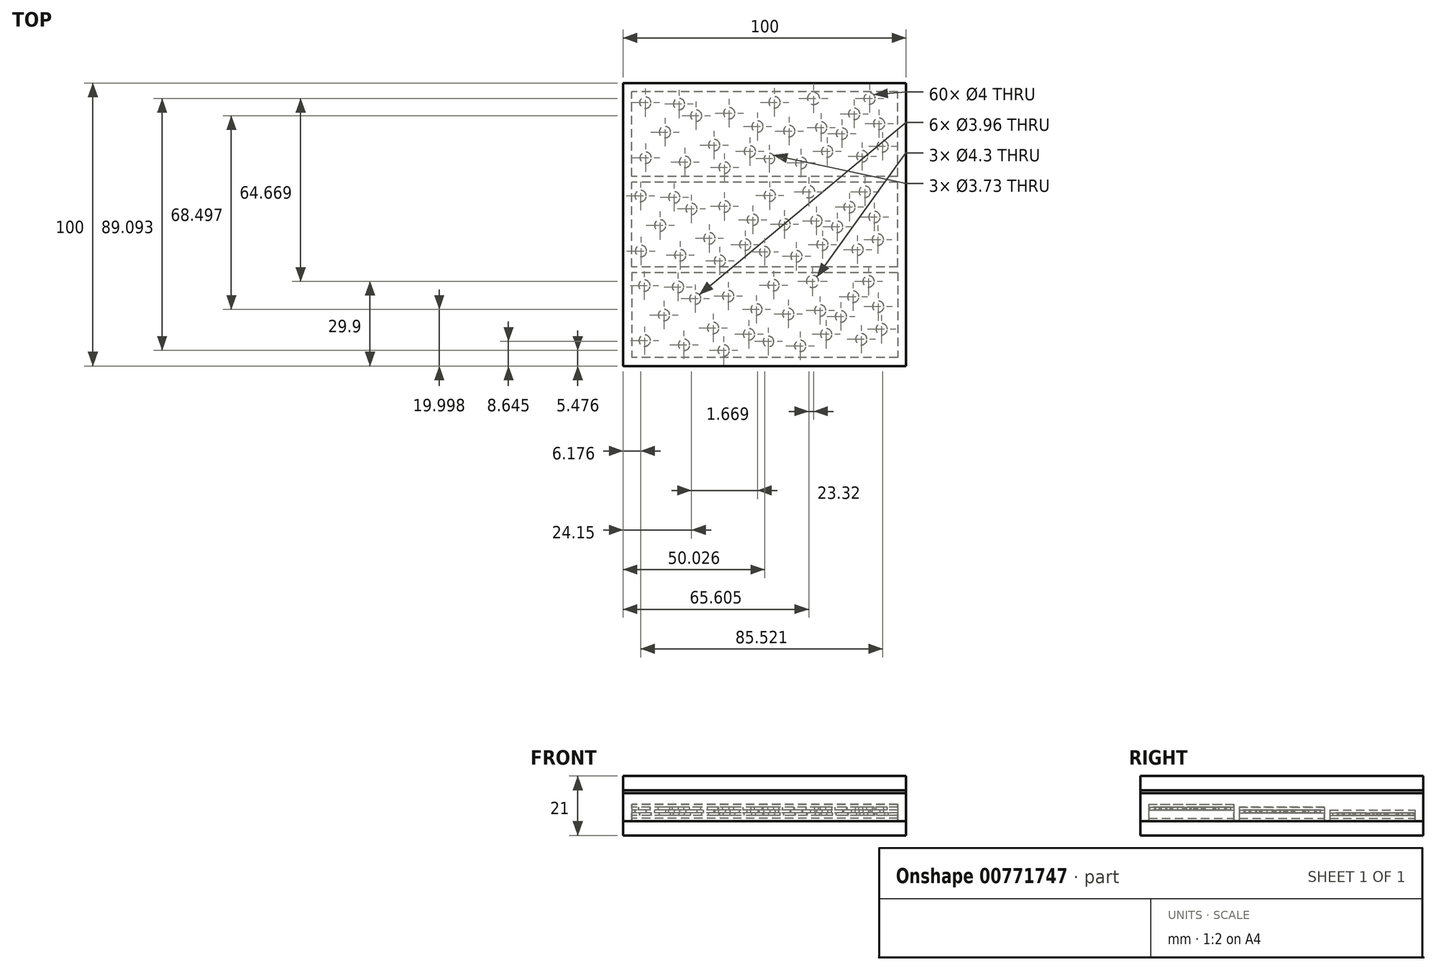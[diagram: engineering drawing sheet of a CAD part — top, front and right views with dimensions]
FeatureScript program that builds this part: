
annotation { "Feature Type Name" : "Feature", "Feature Type Description" : "" }
export const myFeature = defineFeature(function(context is Context, id is Id, definition is map)
    precondition{}
    {
        {
            var Q0;
            Q0=qCreatedBy(makeId("Top.planeOp"),FACE);
            var sketch = newSketch(context, id + "F0", { "sketchPlane" : qUnion([Q0])});
            skLineSegment(sketch, "E0.bottom", {"start": v(50, -50) * mm, "end": v(-50, -50) * mm});
            skLineSegment(sketch, "E0.top", {"start": v(50, 50) * mm, "end": v(-50, 50) * mm});
            skLineSegment(sketch, "E0.left", {"start": v(50, -50) * mm, "end": v(50, 50) * mm});
            skLineSegment(sketch, "E0.right", {"start": v(-50, -50) * mm, "end": v(-50, 50) * mm});
            skPoint(sketch, "E0.middle", {"position": v(0, 0) * mm});
            skSolve(sketch);
        }
        {
            var Q0;
            Q0=makeQuery(id+"F0.imprint","IMPRINT",FACE,{"disambiguationData":[TD([[makeQuery(id+"F0.imprint","IMPRINT",EDGE,{"derivedFrom":sQuery(id+"F0.wireOp",EDGE,"E0.bottom")}),-1.0]])]});
            extrude(context, id + "F1", {"entities" : qUnion([Q0]), "depth" : 5 * mm, "offsetDistance" : 25 * mm});
        }
        {
            var Q0;
            Q0=makeQuery(id+"F1.opExtrude","CAP_FACE",FACE,{"disambiguationData":[OSD([sQuery(id+"F0.wireOp",EDGE,"E0.bottom"),sQuery(id+"F0.wireOp",EDGE,"E0.top"),sQuery(id+"F0.wireOp",EDGE,"E0.left"),sQuery(id+"F0.wireOp",EDGE,"E0.right")])],"isStart":false});
            var sketch = newSketch(context, id + "F2", { "sketchPlane" : qUnion([Q0])});
            skLineSegment(sketch, "E1.bottom", {"start": v(47, -15) * mm, "end": v(-47, -15) * mm});
            skLineSegment(sketch, "E1.top", {"start": v(47, 15) * mm, "end": v(-47, 15) * mm});
            skLineSegment(sketch, "E1.left", {"start": v(47, -15) * mm, "end": v(47, 15) * mm});
            skLineSegment(sketch, "E1.right", {"start": v(-47, -15) * mm, "end": v(-47, 15) * mm});
            skPoint(sketch, "E1.middle", {"position": v(0, 0) * mm});
            skLineSegment(sketch, "E2.bottom", {"start": v(47, 17) * mm, "end": v(-47, 17) * mm});
            skLineSegment(sketch, "E2.top", {"start": v(47, 47) * mm, "end": v(-47, 47) * mm});
            skLineSegment(sketch, "E2.left", {"start": v(47, 17) * mm, "end": v(47, 47) * mm});
            skLineSegment(sketch, "E2.right", {"start": v(-47, 17) * mm, "end": v(-47, 47) * mm});
            skPoint(sketch, "E2.middle", {"position": v(0, 32) * mm});
            skLineSegment(sketch, "E3.bottom", {"start": v(47, -47) * mm, "end": v(-47, -47) * mm});
            skLineSegment(sketch, "E3.top", {"start": v(47, -17) * mm, "end": v(-47, -17) * mm});
            skLineSegment(sketch, "E3.left", {"start": v(47, -47) * mm, "end": v(47, -17) * mm});
            skLineSegment(sketch, "E3.right", {"start": v(-47, -47) * mm, "end": v(-47, -17) * mm});
            skPoint(sketch, "E3.middle", {"position": v(0, -32) * mm});
            skSolve(sketch);
        }
        {
            var Q0;
            Q0=makeQuery(id+"F2.imprint","IMPRINT",FACE,{"disambiguationData":[TD([[makeQuery(id+"F2.imprint","IMPRINT",EDGE,{"derivedFrom":sQuery(id+"F2.wireOp",EDGE,"E2.bottom")}),-1.0]])]});
            var Q1;
            Q1=makeQuery(id+"F2.imprint","IMPRINT",FACE,{"disambiguationData":[TD([[makeQuery(id+"F2.imprint","IMPRINT",EDGE,{"derivedFrom":sQuery(id+"F2.wireOp",EDGE,"E1.bottom")}),-1.0]])]});
            var Q2;
            Q2=makeQuery(id+"F2.imprint","IMPRINT",FACE,{"disambiguationData":[TD([[makeQuery(id+"F2.imprint","IMPRINT",EDGE,{"derivedFrom":sQuery(id+"F2.wireOp",EDGE,"E3.bottom")}),-1.0]])]});
            extrude(context, id + "F3", {"entities" : qUnion([Q0, Q1, Q2]), "depth" : 1 * mm, "offsetDistance" : 25 * mm});
        }
        {
            var Q0;
            Q0=makeQuery(id+"F3.opExtrude","CAP_FACE",FACE,{"disambiguationData":[OSD([sQuery(id+"F2.wireOp",EDGE,"E2.bottom"),sQuery(id+"F2.wireOp",EDGE,"E2.top"),sQuery(id+"F2.wireOp",EDGE,"E2.left"),sQuery(id+"F2.wireOp",EDGE,"E2.right")])],"isStart":false});
            extrude(context, id + "F4", {"entities" : qUnion([Q0]), "depth" : 1 * mm, "offsetDistance" : 25 * mm});
        }
        {
            var Q0;
            Q0=makeQuery(id+"F3.opExtrude","CAP_FACE",FACE,{"disambiguationData":[OSD([sQuery(id+"F2.wireOp",EDGE,"E1.bottom"),sQuery(id+"F2.wireOp",EDGE,"E1.top"),sQuery(id+"F2.wireOp",EDGE,"E1.left"),sQuery(id+"F2.wireOp",EDGE,"E1.right")])],"isStart":false});
            extrude(context, id + "F5", {"entities" : qUnion([Q0]), "depth" : 2 * mm, "offsetDistance" : 25 * mm});
        }
        {
            var Q0;
            Q0=makeQuery(id+"F3.opExtrude","CAP_FACE",FACE,{"disambiguationData":[OSD([sQuery(id+"F2.wireOp",EDGE,"E3.bottom"),sQuery(id+"F2.wireOp",EDGE,"E3.top"),sQuery(id+"F2.wireOp",EDGE,"E3.left"),sQuery(id+"F2.wireOp",EDGE,"E3.right")])],"isStart":false});
            extrude(context, id + "F6", {"entities" : qUnion([Q0]), "depth" : 3 * mm, "offsetDistance" : 25 * mm});
        }
        {
            var Q0;
            Q0=makeQuery(id+"F6.opExtrude","CAP_FACE",FACE,{"disambiguationData":[OSD([sQuery(id+"F2.wireOp",EDGE,"E3.bottom"),sQuery(id+"F2.wireOp",EDGE,"E3.top"),sQuery(id+"F2.wireOp",EDGE,"E3.left"),sQuery(id+"F2.wireOp",EDGE,"E3.right")])],"isStart":false});
            var Q1;
            Q1=makeQuery(id+"F5.opExtrude","CAP_FACE",FACE,{"disambiguationData":[OSD([sQuery(id+"F2.wireOp",EDGE,"E1.bottom"),sQuery(id+"F2.wireOp",EDGE,"E1.top"),sQuery(id+"F2.wireOp",EDGE,"E1.left"),sQuery(id+"F2.wireOp",EDGE,"E1.right")])],"isStart":false});
            var Q2;
            Q2=makeQuery(id+"F4.opExtrude","CAP_FACE",FACE,{"disambiguationData":[OSD([sQuery(id+"F2.wireOp",EDGE,"E2.bottom"),sQuery(id+"F2.wireOp",EDGE,"E2.top"),sQuery(id+"F2.wireOp",EDGE,"E2.left"),sQuery(id+"F2.wireOp",EDGE,"E2.right")])],"isStart":false});
            extrude(context, id + "F7", {"entities" : qUnion([Q0, Q1, Q2]), "depth" : 1 * mm, "offsetDistance" : 25 * mm});
        }
        {
            var Q0;
            Q0=makeQuery(id+"F7.opExtrude","CAP_FACE",FACE,{"disambiguationData":[OSD([sQuery(id+"F2.wireOp",EDGE,"E3.bottom"),sQuery(id+"F2.wireOp",EDGE,"E3.top"),sQuery(id+"F2.wireOp",EDGE,"E3.left"),sQuery(id+"F2.wireOp",EDGE,"E3.right")])],"isStart":false});
            var sketch = newSketch(context, id + "F8", { "sketchPlane" : qUnion([Q0])});
            skCircle(sketch, "E4", {"center": v(-35.55, -32) * mm, "radius": 2 * mm});
            skCircle(sketch, "E5", {"center": v(-18.19, -36.58) * mm, "radius": 2 * mm});
            skCircle(sketch, "E6", {"center": v(-12.85, -25.3) * mm, "radius": 2 * mm});
            skCircle(sketch, "E7", {"center": v(8.36, -31.62) * mm, "radius": 2 * mm});
            skCircle(sketch, "E8", {"center": v(19.64, -30.38) * mm, "radius": 2 * mm});
            skCircle(sketch, "E9", {"center": v(31.3, -25.54) * mm, "radius": 2 * mm});
            skCircle(sketch, "E10", {"center": v(34.16, -40.55) * mm, "radius": 2 * mm});
            skCircle(sketch, "E11", {"center": v(12.57, -42.9) * mm, "radius": 2 * mm});
            skCircle(sketch, "E12", {"center": v(3.15, -21.45) * mm, "radius": 2 * mm});
            skCircle(sketch, "E13", {"center": v(-5.53, -38.81) * mm, "radius": 2 * mm});
            skCircle(sketch, "E14", {"center": v(-30.59, -22.07) * mm, "radius": 2 * mm});
            skCircle(sketch, "E15", {"center": v(-42.37, -41.05) * mm, "radius": 2 * mm});
            skCircle(sketch, "E16", {"center": v(40.11, -29.01) * mm, "radius": 2 * mm});
            skCircle(sketch, "E17", {"center": v(-28.48, -42.53) * mm, "radius": 2 * mm});
            skCircle(sketch, "E18", {"center": v(21.75, -38.81) * mm, "radius": 2 * mm});
            skCircle(sketch, "E19", {"center": v(-42.5, -21.57) * mm, "radius": 2 * mm});
            skCircle(sketch, "E20", {"center": v(-2.87, -30) * mm, "radius": 1.98 * mm});
            skCircle(sketch, "E21", {"center": v(16.93, -20.1) * mm, "radius": 2.15 * mm});
            skCircle(sketch, "E22", {"center": v(-24.52, -26.17) * mm, "radius": 1.98 * mm});
            skCircle(sketch, "E23", {"center": v(36.73, -20.1) * mm, "radius": 2 * mm});
            skCircle(sketch, "E24", {"center": v(41.36, -37) * mm, "radius": 2 * mm});
            skCircle(sketch, "E25", {"center": v(26.97, -32.5) * mm, "radius": 2 * mm});
            skCircle(sketch, "E26", {"center": v(1.35, -41.36) * mm, "radius": 1.87 * mm});
            skCircle(sketch, "E27", {"center": v(-14.49, -44.52) * mm, "radius": 2 * mm});
            skSolve(sketch);
        }
        {
            var Q0;
            Q0=qSketchRegion(id+"F8",true);
            extrude(context, id + "F9", {"entities" : qUnion([Q0]), "operationType" : NewBodyOperationType.REMOVE, "oppositeDirection" : true, "depth" : 1 * mm, "offsetDistance" : 25 * mm});
        }
        {
            var Q0;
            Q0=makeQuery(id+"F7.opExtrude","CAP_FACE",FACE,{"disambiguationData":[OSD([sQuery(id+"F2.wireOp",EDGE,"E1.bottom"),sQuery(id+"F2.wireOp",EDGE,"E1.top"),sQuery(id+"F2.wireOp",EDGE,"E1.left"),sQuery(id+"F2.wireOp",EDGE,"E1.right")])],"isStart":false});
            var sketch = newSketch(context, id + "F10", { "sketchPlane" : qUnion([Q0])});
            skCircle(sketch, "E28", {"center": v(-36.88, -0.3) * mm, "radius": 2 * mm});
            skCircle(sketch, "E29", {"center": v(-19.51, -4.9) * mm, "radius": 2 * mm});
            skCircle(sketch, "E30", {"center": v(-14.18, 6.4) * mm, "radius": 2 * mm});
            skCircle(sketch, "E31", {"center": v(7.03, 0.07) * mm, "radius": 2 * mm});
            skCircle(sketch, "E32", {"center": v(18.32, 1.3) * mm, "radius": 2 * mm});
            skCircle(sketch, "E33", {"center": v(29.98, 6.15) * mm, "radius": 2 * mm});
            skCircle(sketch, "E34", {"center": v(32.83, -8.86) * mm, "radius": 2 * mm});
            skCircle(sketch, "E35", {"center": v(11.25, -11.22) * mm, "radius": 2 * mm});
            skCircle(sketch, "E36", {"center": v(1.82, 10.24) * mm, "radius": 2 * mm});
            skCircle(sketch, "E37", {"center": v(-6.86, -7.13) * mm, "radius": 2 * mm});
            skCircle(sketch, "E38", {"center": v(-31.92, 9.62) * mm, "radius": 2 * mm});
            skCircle(sketch, "E39", {"center": v(-43.7, -9.36) * mm, "radius": 2 * mm});
            skCircle(sketch, "E40", {"center": v(38.78, 2.67) * mm, "radius": 2 * mm});
            skCircle(sketch, "E41", {"center": v(-29.8, -10.85) * mm, "radius": 2 * mm});
            skCircle(sketch, "E42", {"center": v(20.43, -7.13) * mm, "radius": 2 * mm});
            skCircle(sketch, "E43", {"center": v(-43.82, 10.12) * mm, "radius": 2 * mm});
            skCircle(sketch, "E44", {"center": v(-4.2, 1.69) * mm, "radius": 1.98 * mm});
            skCircle(sketch, "E45", {"center": v(15.6, 11.59) * mm, "radius": 2.15 * mm});
            skCircle(sketch, "E46", {"center": v(-25.85, 5.52) * mm, "radius": 1.98 * mm});
            skCircle(sketch, "E47", {"center": v(35.4, 11.59) * mm, "radius": 2 * mm});
            skCircle(sketch, "E48", {"center": v(40.03, -5.31) * mm, "radius": 2 * mm});
            skCircle(sketch, "E49", {"center": v(25.64, -0.82) * mm, "radius": 2 * mm});
            skCircle(sketch, "E50", {"center": v(0.03, -9.67) * mm, "radius": 1.87 * mm});
            skCircle(sketch, "E51", {"center": v(-15.82, -12.84) * mm, "radius": 2 * mm});
            skSolve(sketch);
        }
        {
            var Q0;
            Q0=qSketchRegion(id+"F10",true);
            extrude(context, id + "F11", {"entities" : qUnion([Q0]), "operationType" : NewBodyOperationType.REMOVE, "oppositeDirection" : true, "depth" : 1 * mm, "offsetDistance" : 25 * mm});
        }
        {
            var Q0;
            Q0=makeQuery(id+"F7.opExtrude","CAP_FACE",FACE,{"disambiguationData":[OSD([sQuery(id+"F2.wireOp",EDGE,"E2.bottom"),sQuery(id+"F2.wireOp",EDGE,"E2.top"),sQuery(id+"F2.wireOp",EDGE,"E2.left"),sQuery(id+"F2.wireOp",EDGE,"E2.right")])],"isStart":false});
            var sketch = newSketch(context, id + "F12", { "sketchPlane" : qUnion([Q0])});
            skCircle(sketch, "E52", {"center": v(-35.2, 32.68) * mm, "radius": 2 * mm});
            skCircle(sketch, "E53", {"center": v(-17.84, 28.09) * mm, "radius": 2 * mm});
            skCircle(sketch, "E54", {"center": v(-12.51, 39.38) * mm, "radius": 2 * mm});
            skCircle(sketch, "E55", {"center": v(8.7, 33.05) * mm, "radius": 2 * mm});
            skCircle(sketch, "E56", {"center": v(19.99, 34.29) * mm, "radius": 2 * mm});
            skCircle(sketch, "E57", {"center": v(31.65, 39.13) * mm, "radius": 2 * mm});
            skCircle(sketch, "E58", {"center": v(34.5, 24.12) * mm, "radius": 2 * mm});
            skCircle(sketch, "E59", {"center": v(12.92, 21.76) * mm, "radius": 2 * mm});
            skCircle(sketch, "E60", {"center": v(3.49, 43.22) * mm, "radius": 2 * mm});
            skCircle(sketch, "E61", {"center": v(-5.2, 25.86) * mm, "radius": 2 * mm});
            skCircle(sketch, "E62", {"center": v(-30.25, 42.6) * mm, "radius": 2 * mm});
            skCircle(sketch, "E63", {"center": v(-42.03, 23.62) * mm, "radius": 2 * mm});
            skCircle(sketch, "E64", {"center": v(40.45, 35.65) * mm, "radius": 2 * mm});
            skCircle(sketch, "E65", {"center": v(-28.14, 22.13) * mm, "radius": 2 * mm});
            skCircle(sketch, "E66", {"center": v(22.1, 25.86) * mm, "radius": 2 * mm});
            skCircle(sketch, "E67", {"center": v(-42.16, 43.1) * mm, "radius": 2 * mm});
            skCircle(sketch, "E68", {"center": v(-2.53, 34.67) * mm, "radius": 1.98 * mm});
            skCircle(sketch, "E69", {"center": v(17.27, 44.57) * mm, "radius": 2.15 * mm});
            skCircle(sketch, "E70", {"center": v(-24.18, 38.5) * mm, "radius": 1.98 * mm});
            skCircle(sketch, "E71", {"center": v(37.08, 44.57) * mm, "radius": 2 * mm});
            skCircle(sketch, "E72", {"center": v(41.7, 27.67) * mm, "radius": 2 * mm});
            skCircle(sketch, "E73", {"center": v(27.3, 32.16) * mm, "radius": 2 * mm});
            skCircle(sketch, "E74", {"center": v(1.7, 23.31) * mm, "radius": 1.87 * mm});
            skCircle(sketch, "E75", {"center": v(-14.15, 20.14) * mm, "radius": 2 * mm});
            skSolve(sketch);
        }
        {
            var Q0;
            Q0=qSketchRegion(id+"F12",true);
            extrude(context, id + "F13", {"entities" : qUnion([Q0]), "operationType" : NewBodyOperationType.REMOVE, "oppositeDirection" : true, "depth" : 1 * mm, "offsetDistance" : 25 * mm});
        }
        {
            var Q0;
            Q0=makeQuery(id+"F7.opExtrude","CAP_FACE",FACE,{"disambiguationData":[OSD([sQuery(id+"F2.wireOp",EDGE,"E2.bottom"),sQuery(id+"F2.wireOp",EDGE,"E2.top"),sQuery(id+"F2.wireOp",EDGE,"E2.left"),sQuery(id+"F2.wireOp",EDGE,"E2.right")])],"isStart":false});
            var sketch = newSketch(context, id + "F14", { "sketchPlane" : qUnion([Q0])});
            skLineSegment(sketch, "E76.bottom", {"start": v(47, 17) * mm, "end": v(-47, 17) * mm});
            skLineSegment(sketch, "E76.top", {"start": v(47, 47) * mm, "end": v(-47, 47) * mm});
            skLineSegment(sketch, "E76.left", {"start": v(47, 17) * mm, "end": v(47, 47) * mm});
            skLineSegment(sketch, "E76.right", {"start": v(-47, 17) * mm, "end": v(-47, 47) * mm});
            skPoint(sketch, "E76.middle", {"position": v(0, 32) * mm});
            skSolve(sketch);
        }
        {
            var Q0;
            Q0=qSketchRegion(id+"F14",true);
            extrude(context, id + "F15", {"entities" : qUnion([Q0]), "depth" : 1 * mm, "offsetDistance" : 25 * mm});
        }
        {
            var Q0;
            Q0=makeQuery(id+"F7.opExtrude","CAP_FACE",FACE,{"disambiguationData":[OSD([sQuery(id+"F2.wireOp",EDGE,"E1.bottom"),sQuery(id+"F2.wireOp",EDGE,"E1.top"),sQuery(id+"F2.wireOp",EDGE,"E1.left"),sQuery(id+"F2.wireOp",EDGE,"E1.right")])],"isStart":false});
            var sketch = newSketch(context, id + "F16", { "sketchPlane" : qUnion([Q0])});
            skLineSegment(sketch, "E77.bottom", {"start": v(-47, -15) * mm, "end": v(47, -15) * mm});
            skLineSegment(sketch, "E77.top", {"start": v(-47, 15) * mm, "end": v(47, 15) * mm});
            skLineSegment(sketch, "E77.left", {"start": v(-47, -15) * mm, "end": v(-47, 15) * mm});
            skLineSegment(sketch, "E77.right", {"start": v(47, -15) * mm, "end": v(47, 15) * mm});
            skPoint(sketch, "E77.middle", {"position": v(0, 0) * mm});
            skSolve(sketch);
        }
        {
            var Q0;
            Q0=qSketchRegion(id+"F16",true);
            extrude(context, id + "F17", {"entities" : qUnion([Q0]), "depth" : 1 * mm, "offsetDistance" : 25 * mm});
        }
        {
            var Q0;
            Q0=makeQuery(id+"F7.opExtrude","CAP_FACE",FACE,{"disambiguationData":[OSD([sQuery(id+"F2.wireOp",EDGE,"E3.bottom"),sQuery(id+"F2.wireOp",EDGE,"E3.top"),sQuery(id+"F2.wireOp",EDGE,"E3.left"),sQuery(id+"F2.wireOp",EDGE,"E3.right")])],"isStart":false});
            var sketch = newSketch(context, id + "F18", { "sketchPlane" : qUnion([Q0])});
            skLineSegment(sketch, "E78.bottom", {"start": v(47, -47) * mm, "end": v(-47, -47) * mm});
            skLineSegment(sketch, "E78.top", {"start": v(47, -17) * mm, "end": v(-47, -17) * mm});
            skLineSegment(sketch, "E78.left", {"start": v(47, -47) * mm, "end": v(47, -17) * mm});
            skLineSegment(sketch, "E78.right", {"start": v(-47, -47) * mm, "end": v(-47, -17) * mm});
            skPoint(sketch, "E78.middle", {"position": v(0, -32) * mm});
            skSolve(sketch);
        }
        {
            var Q0;
            Q0=qSketchRegion(id+"F18",true);
            extrude(context, id + "F19", {"entities" : qUnion([Q0]), "depth" : 1 * mm, "offsetDistance" : 25 * mm});
        }
        {
            var Q0;
            Q0=makeQuery(id+"F15.opExtrude","SWEPT_FACE",FACE,{"disambiguationData":[OSD([sQuery(id+"F14.wireOp",EDGE,"E76.right")])]});
            var sketch = newSketch(context, id + "F20", { "sketchPlane" : qUnion([Q0])});
            skLineSegment(sketch, "E79", {"start": v(-50, 5) * mm, "end": v(-47, 5) * mm});
            skLineSegment(sketch, "E80", {"start": v(-47, 5) * mm, "end": v(-47, 8.94) * mm});
            skLineSegment(sketch, "E81", {"start": v(-47, 8.94) * mm, "end": v(-17, 8.94) * mm});
            skLineSegment(sketch, "E82", {"start": v(-17, 8.94) * mm, "end": v(-17, 5) * mm});
            skLineSegment(sketch, "E83", {"start": v(-17, 5) * mm, "end": v(-15, 5) * mm});
            skLineSegment(sketch, "E84", {"start": v(-15, 5) * mm, "end": v(-15, 10.02) * mm});
            skLineSegment(sketch, "E85", {"start": v(-15, 10.02) * mm, "end": v(15, 10.02) * mm});
            skLineSegment(sketch, "E86", {"start": v(15, 10.02) * mm, "end": v(15, 5) * mm});
            skLineSegment(sketch, "E87", {"start": v(15, 5) * mm, "end": v(17, 5) * mm});
            skLineSegment(sketch, "E88", {"start": v(17, 5) * mm, "end": v(17, 10.88) * mm});
            skLineSegment(sketch, "E89", {"start": v(17, 10.88) * mm, "end": v(47, 10.88) * mm});
            skLineSegment(sketch, "E90", {"start": v(47, 10.88) * mm, "end": v(47, 5) * mm});
            skLineSegment(sketch, "E91", {"start": v(47, 5) * mm, "end": v(50, 5) * mm});
            skLineSegment(sketch, "E92", {"start": v(50, 5) * mm, "end": v(50, 15) * mm});
            skLineSegment(sketch, "E93", {"start": v(50, 15) * mm, "end": v(-50, 15) * mm});
            skLineSegment(sketch, "E94", {"start": v(-50, 15) * mm, "end": v(-50, 5) * mm});
            skSolve(sketch);
        }
        {
            var Q0;
            {var subQ8=sQuery(id+"F20.wireOp",EDGE,"E79");Q0=makeQuery(id+"F20.imprint","IMPRINT",FACE,{"disambiguationData":[TD([[makeQuery(id+"F20.imprint","IMPRINT",EDGE,{"derivedFrom":subQ8}),1.0]])]});}
            extrude(context, id + "F21", {"entities" : qUnion([Q0]), "oppositeDirection" : true, "depth" : 94 * mm, "offsetDistance" : 25 * mm});
        }
        {
            var Q0;
            Q0=makeQuery(id+"F1.opExtrude","CAP_FACE",FACE,{"disambiguationData":[OSD([sQuery(id+"F0.wireOp",EDGE,"E0.bottom"),sQuery(id+"F0.wireOp",EDGE,"E0.top"),sQuery(id+"F0.wireOp",EDGE,"E0.left"),sQuery(id+"F0.wireOp",EDGE,"E0.right")])],"isStart":false});
            var sketch = newSketch(context, id + "F22", { "sketchPlane" : qUnion([Q0])});
            skLineSegment(sketch, "E95.bottom", {"start": v(-50, 50) * mm, "end": v(-47, 50) * mm});
            skLineSegment(sketch, "E95.top", {"start": v(-50, -50) * mm, "end": v(-47, -50) * mm});
            skLineSegment(sketch, "E95.left", {"start": v(-50, 50) * mm, "end": v(-50, -50) * mm});
            skLineSegment(sketch, "E95.right", {"start": v(-47, 50) * mm, "end": v(-47, -50) * mm});
            skLineSegment(sketch, "E96.bottom", {"start": v(47, 50) * mm, "end": v(50, 50) * mm});
            skLineSegment(sketch, "E96.top", {"start": v(47, -50) * mm, "end": v(50, -50) * mm});
            skLineSegment(sketch, "E96.left", {"start": v(47, 50) * mm, "end": v(47, -50) * mm});
            skLineSegment(sketch, "E96.right", {"start": v(50, 50) * mm, "end": v(50, -50) * mm});
            skSolve(sketch);
        }
        {
            var Q0;
            Q0=makeQuery(id+"F22.imprint","IMPRINT",FACE,{"disambiguationData":[TD([[makeQuery(id+"F22.imprint","IMPRINT",EDGE,{"derivedFrom":sQuery(id+"F22.wireOp",EDGE,"E95.bottom")}),1.0]])]});
            var Q1;
            Q1=makeQuery(id+"F22.imprint","IMPRINT",FACE,{"disambiguationData":[TD([[makeQuery(id+"F22.imprint","IMPRINT",EDGE,{"derivedFrom":sQuery(id+"F22.wireOp",EDGE,"E96.bottom")}),1.0]])]});
            extrude(context, id + "F23", {"entities" : qUnion([Q0, Q1]), "depth" : 10 * mm, "offsetDistance" : 25 * mm});
        }
        {
            var Q0;
            Q0=makeQuery(id+"F21.opExtrude","SWEPT_BODY",BODY,{"disambiguationData":[OSD([sQuery(id+"F14.wireOp",EDGE,"E76.bottom"),sQuery(id+"F14.wireOp",EDGE,"E76.top"),sQuery(id+"F14.wireOp",EDGE,"E76.right"),sQuery(id+"F20.wireOp",EDGE,"E79"),sQuery(id+"F20.wireOp",EDGE,"E80"),sQuery(id+"F20.wireOp",EDGE,"E82"),sQuery(id+"F20.wireOp",EDGE,"E83"),sQuery(id+"F20.wireOp",EDGE,"E84"),sQuery(id+"F20.wireOp",EDGE,"E85"),sQuery(id+"F20.wireOp",EDGE,"E86"),sQuery(id+"F20.wireOp",EDGE,"E87"),sQuery(id+"F20.wireOp",EDGE,"E88"),sQuery(id+"F20.wireOp",EDGE,"E89"),sQuery(id+"F20.wireOp",EDGE,"E90"),sQuery(id+"F20.wireOp",EDGE,"E91"),sQuery(id+"F20.wireOp",EDGE,"E92"),sQuery(id+"F20.wireOp",EDGE,"E93"),sQuery(id+"F20.wireOp",EDGE,"E94")])]});
            var Q1;
            Q1=makeQuery(id+"F23.opExtrude","SWEPT_BODY",BODY,{"disambiguationData":[OSD([sQuery(id+"F22.wireOp",EDGE,"E95.bottom"),sQuery(id+"F22.wireOp",EDGE,"E95.top"),sQuery(id+"F22.wireOp",EDGE,"E95.left"),sQuery(id+"F22.wireOp",EDGE,"E95.right")])]});
            var Q2;
            Q2=makeQuery(id+"F23.opExtrude","SWEPT_BODY",BODY,{"disambiguationData":[OSD([sQuery(id+"F22.wireOp",EDGE,"E96.bottom"),sQuery(id+"F22.wireOp",EDGE,"E96.top"),sQuery(id+"F22.wireOp",EDGE,"E96.left"),sQuery(id+"F22.wireOp",EDGE,"E96.right")])]});
            booleanBodies(context, id + "F24", {"operationType" : BooleanOperationType.UNION, "tools" : qUnion([Q0, Q1, Q2])});
        }
        {
            var Q0;
            Q0=makeQuery(id+"F24.opBoolean","MERGE",FACE,{"derivedFrom":[makeQuery(id+"F21.opExtrude","SWEPT_FACE",FACE,{"disambiguationData":[OSD([sQuery(id+"F20.wireOp",EDGE,"E93")])]}),makeQuery(id+"F23.opExtrude","CAP_FACE",FACE,{"disambiguationData":[OSD([sQuery(id+"F22.wireOp",EDGE,"E95.bottom"),sQuery(id+"F22.wireOp",EDGE,"E95.top"),sQuery(id+"F22.wireOp",EDGE,"E95.left"),sQuery(id+"F22.wireOp",EDGE,"E95.right")])],"isStart":false}),makeQuery(id+"F23.opExtrude","CAP_FACE",FACE,{"disambiguationData":[OSD([sQuery(id+"F22.wireOp",EDGE,"E96.bottom"),sQuery(id+"F22.wireOp",EDGE,"E96.top"),sQuery(id+"F22.wireOp",EDGE,"E96.left"),sQuery(id+"F22.wireOp",EDGE,"E96.right")])],"isStart":false})]});
            extrude(context, id + "F25", {"entities" : qUnion([Q0]), "depth" : 1 * mm, "offsetDistance" : 25 * mm});
        }
        {
            var Q0;
            Q0=makeQuery(id+"F25.opExtrude","CAP_FACE",FACE,{"disambiguationData":[OSD([sQuery(id+"F20.wireOp",EDGE,"E93"),sQuery(id+"F22.wireOp",EDGE,"E95.bottom"),sQuery(id+"F22.wireOp",EDGE,"E95.top"),sQuery(id+"F22.wireOp",EDGE,"E95.left"),sQuery(id+"F22.wireOp",EDGE,"E95.right"),sQuery(id+"F22.wireOp",EDGE,"E96.bottom"),sQuery(id+"F22.wireOp",EDGE,"E96.top"),sQuery(id+"F22.wireOp",EDGE,"E96.left"),sQuery(id+"F22.wireOp",EDGE,"E96.right")])],"isStart":false});
            extrude(context, id + "F26", {"entities" : qUnion([Q0]), "depth" : 5 * mm, "offsetDistance" : 25 * mm});
        }
    });
